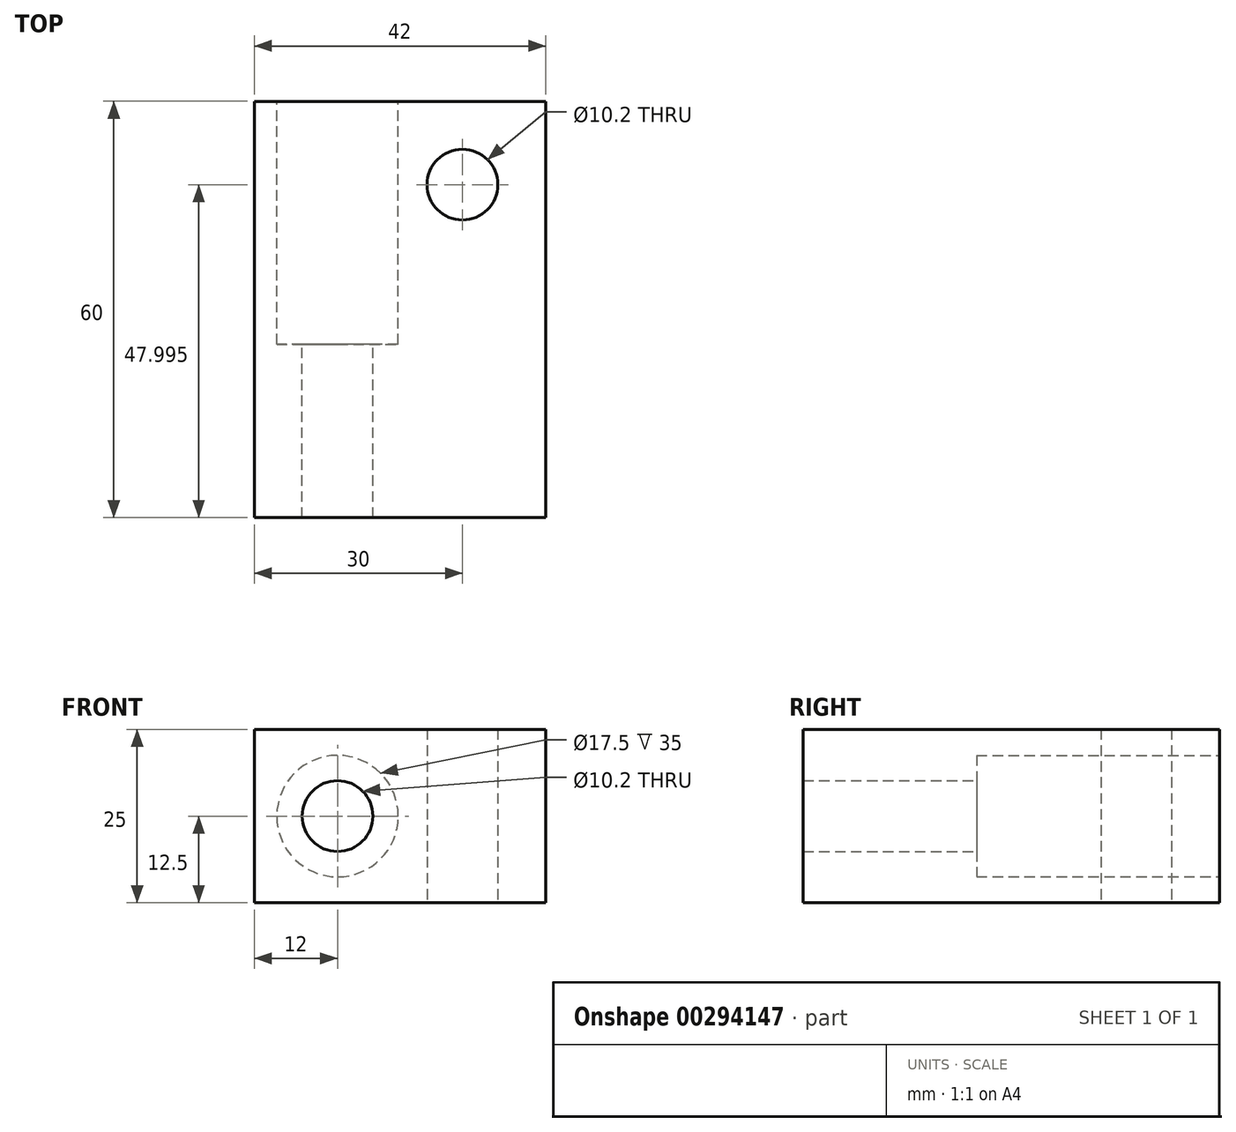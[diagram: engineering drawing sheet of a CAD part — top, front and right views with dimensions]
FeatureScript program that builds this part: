
annotation { "Feature Type Name" : "Feature", "Feature Type Description" : "" }
export const myFeature = defineFeature(function(context is Context, id is Id, definition is map)
    precondition{}
    {
        {
            var Q0;
            Q0=qCreatedBy(makeId("Top.planeOp"),FACE);
            var sketch = newSketch(context, id + "F0", { "sketchPlane" : qUnion([Q0])});
            skLineSegment(sketch, "E0", {"start": v(-42, 17.46) * mm, "end": v(-42, -42.54) * mm});
            skLineSegment(sketch, "E1", {"start": v(-42, -42.54) * mm, "end": v(0, -42.54) * mm});
            skLineSegment(sketch, "E2", {"start": v(0, -42.54) * mm, "end": v(0, 17.46) * mm});
            skLineSegment(sketch, "E3", {"start": v(0, 17.46) * mm, "end": v(-42, 17.46) * mm});
            skCircle(sketch, "E4", {"center": v(-12, 5.46) * mm, "radius": 5.1 * mm});
            skSolve(sketch);
        }
        {
            var Q0;
            Q0=makeQuery(id+"F0.imprint","IMPRINT",FACE,{"disambiguationData":[TD([[makeQuery(id+"F0.imprint","IMPRINT",EDGE,{"derivedFrom":sQuery(id+"F0.wireOp",EDGE,"E0")}),1.0]])]});
            extrude(context, id + "F1", {"entities" : qUnion([Q0]), "depth" : 25 * mm});
        }
        {
            var Q0;
            Q0=makeQuery(id+"F1.opExtrude","SWEPT_FACE",FACE,{"disambiguationData":[OSD([sQuery(id+"F0.wireOp",EDGE,"E3")])]});
            var sketch = newSketch(context, id + "F2", { "sketchPlane" : qUnion([Q0])});
            skCircle(sketch, "E5", {"center": v(30, 12.5) * mm, "radius": 8.75 * mm});
            skCircle(sketch, "E6", {"center": v(30, 12.5) * mm, "radius": 5.1 * mm});
            skSolve(sketch);
        }
        {
            var Q0;
            Q0=makeQuery(id+"F2.imprint","IMPRINT",FACE,{"disambiguationData":[TD([[makeQuery(id+"F2.imprint","IMPRINT",EDGE,{"derivedFrom":sQuery(id+"F2.wireOp",EDGE,"E5")}),1.0]])]});
            extrude(context, id + "F3", {"entities" : qUnion([Q0]), "operationType" : NewBodyOperationType.REMOVE, "oppositeDirection" : true, "depth" : 35 * mm});
        }
        {
            var Q0;
            Q0=makeQuery(id+"F2.imprint","IMPRINT",FACE,{"disambiguationData":[TD([[makeQuery(id+"F2.imprint","IMPRINT",EDGE,{"derivedFrom":sQuery(id+"F2.wireOp",EDGE,"E6")}),1.0]])]});
            extrude(context, id + "F4", {"entities" : qUnion([Q0]), "operationType" : NewBodyOperationType.REMOVE, "oppositeDirection" : true, "depth" : 60 * mm});
        }
    });
